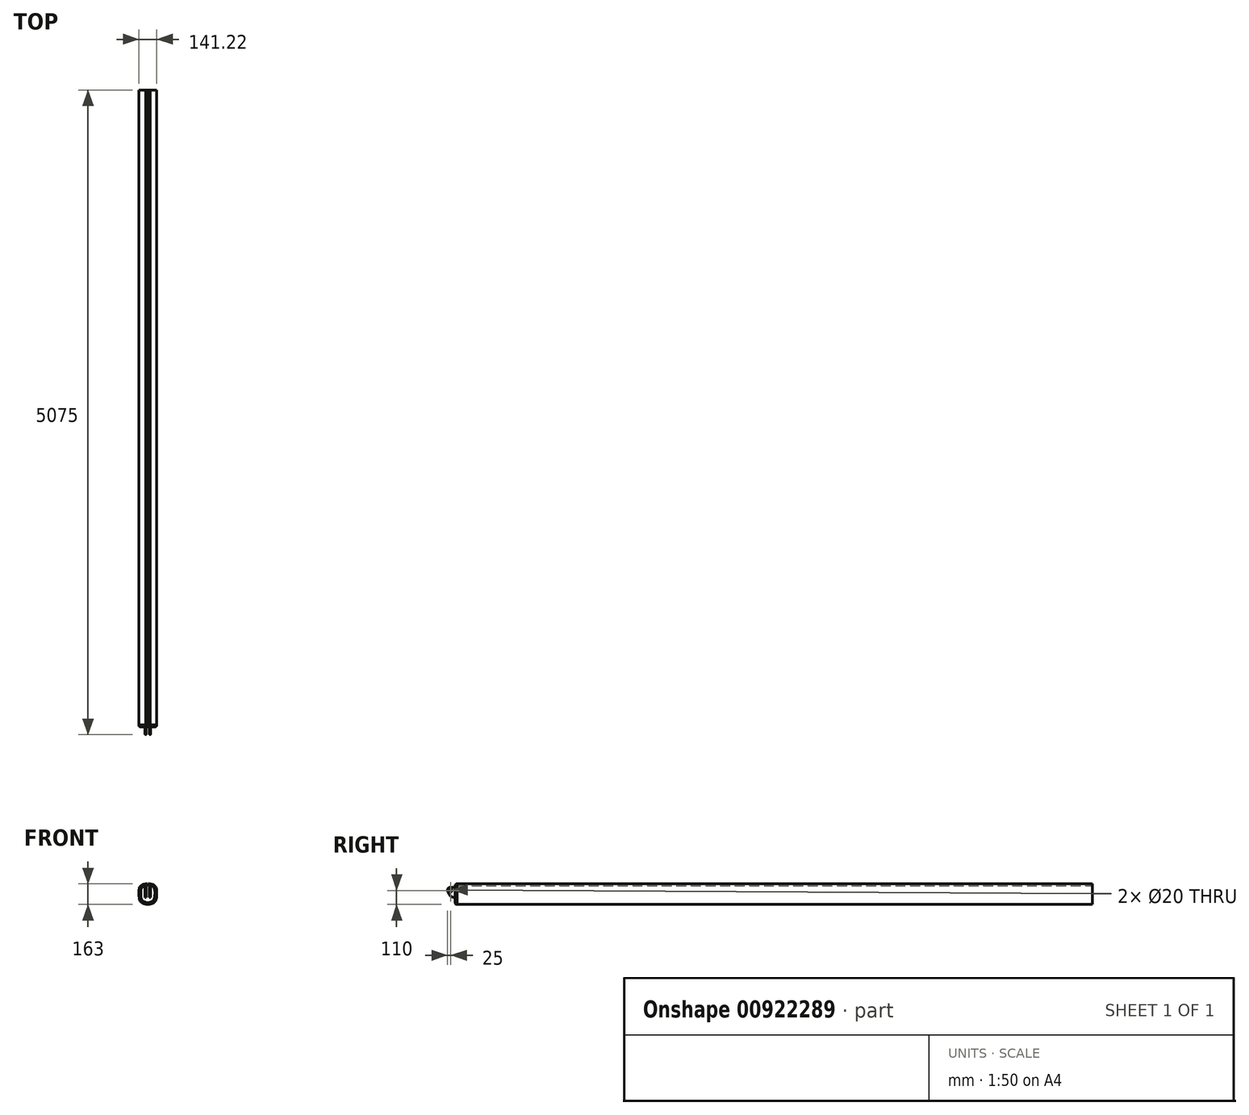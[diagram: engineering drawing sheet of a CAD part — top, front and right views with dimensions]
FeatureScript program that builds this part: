
annotation { "Feature Type Name" : "Feature", "Feature Type Description" : "" }
export const myFeature = defineFeature(function(context is Context, id is Id, definition is map)
    precondition{}
    {
        {
            var Q0;
            Q0=qCreatedBy(makeId("Front.planeOp"),FACE);
            var sketch = newSketch(context, id + "F0", { "sketchPlane" : qUnion([Q0])});
            skLineSegment(sketch, "E0", {"start": v(0, 75) * mm, "end": v(-5, 75) * mm});
            skLineSegment(sketch, "E1", {"start": v(-5, 75) * mm, "end": v(-5, 85) * mm});
            skLineSegment(sketch, "E2", {"start": v(-5, 85) * mm, "end": v(-2.5, 85) * mm});
            skLineSegment(sketch, "E3", {"start": v(-2.5, 85) * mm, "end": v(-2.5, 88) * mm});
            skLineSegment(sketch, "E4", {"start": v(-2.5, 88) * mm, "end": v(-17.5, 88) * mm});
            skFitSpline(sketch, "E5", {"points": [v(-17.5, 88) * mm, v(-62, 61.92) * mm, v(-70.21, 31.1) * mm, v(-64.87, -35.07) * mm, v(-48.84, -59.32) * mm, v(0, -75) * mm], "startDerivative": vector(-363.28, -8.37) * mm, "endDerivative": vector(330.1, 3.15) * mm});
            skLineSegment(sketch, "E6.MirrorCS", {"start": v(2.5, 85) * mm, "end": v(2.5, 88) * mm});
            skLineSegment(sketch, "E7.MirrorCS", {"start": v(5, 85) * mm, "end": v(2.5, 85) * mm});
            skLineSegment(sketch, "E8.MirrorCS", {"start": v(0, 75) * mm, "end": v(5, 75) * mm});
            skLineSegment(sketch, "E9.MirrorCS", {"start": v(2.5, 88) * mm, "end": v(17.5, 88) * mm});
            skLineSegment(sketch, "E10.MirrorCS", {"start": v(5, 75) * mm, "end": v(5, 85) * mm});
            skFitSpline(sketch, "E11.MirrorCS", {"points": [v(17.5, 88) * mm, v(62, 61.92) * mm, v(70.21, 31.1) * mm, v(64.87, -35.07) * mm, v(48.84, -59.32) * mm, v(0, -75) * mm], "startDerivative": vector(363.28, -8.37) * mm, "endDerivative": vector(-330.1, 3.15) * mm});
            skSolve(sketch);
        }
        {
            var Q0;
            Q0=makeQuery(id+"F0.imprint","IMPRINT",FACE,{"disambiguationData":[TD([[makeQuery(id+"F0.imprint","IMPRINT",EDGE,{"derivedFrom":sQuery(id+"F0.wireOp",EDGE,"E0")}),1.0]])]});
            extrude(context, id + "F1", {"entities" : qUnion([Q0]), "depth" : 5000 * mm, "offsetDistance" : 25 * mm, "symmetric" : true});
        }
        {
            var Q0;
            Q0=makeQuery(id+"F1.opExtrude","CAP_FACE",FACE,{"disambiguationData":[OSD([sQuery(id+"F0.wireOp",EDGE,"E0"),sQuery(id+"F0.wireOp",EDGE,"E1"),sQuery(id+"F0.wireOp",EDGE,"E2"),sQuery(id+"F0.wireOp",EDGE,"E3"),sQuery(id+"F0.wireOp",EDGE,"E4"),sQuery(id+"F0.wireOp",EDGE,"E5"),sQuery(id+"F0.wireOp",EDGE,"E6.MirrorCS"),sQuery(id+"F0.wireOp",EDGE,"E7.MirrorCS"),sQuery(id+"F0.wireOp",EDGE,"E8.MirrorCS"),sQuery(id+"F0.wireOp",EDGE,"E9.MirrorCS"),sQuery(id+"F0.wireOp",EDGE,"E10.MirrorCS"),sQuery(id+"F0.wireOp",EDGE,"E11.MirrorCS")])],"isStart":true});
            shell(context, id + "F2", {"entities" : qUnion([Q0]), "thickness" : 4 * mm});
        }
        {
            var Q0;
            Q0=makeQuery(id+"F1.opExtrude","CAP_FACE",FACE,{"disambiguationData":[OSD([sQuery(id+"F0.wireOp",EDGE,"E0"),sQuery(id+"F0.wireOp",EDGE,"E1"),sQuery(id+"F0.wireOp",EDGE,"E2"),sQuery(id+"F0.wireOp",EDGE,"E3"),sQuery(id+"F0.wireOp",EDGE,"E4"),sQuery(id+"F0.wireOp",EDGE,"E5"),sQuery(id+"F0.wireOp",EDGE,"E6.MirrorCS"),sQuery(id+"F0.wireOp",EDGE,"E7.MirrorCS"),sQuery(id+"F0.wireOp",EDGE,"E8.MirrorCS"),sQuery(id+"F0.wireOp",EDGE,"E9.MirrorCS"),sQuery(id+"F0.wireOp",EDGE,"E10.MirrorCS"),sQuery(id+"F0.wireOp",EDGE,"E11.MirrorCS")])],"isStart":false});
            extrude(context, id + "F3", {"entities" : qUnion([Q0]), "depth" : 15 * mm, "offsetDistance" : 25 * mm});
        }
        {
            var Q0;
            Q0=makeQuery(id+"F3.opExtrude","CAP_EDGE",EDGE,{"disambiguationData":[OSD([sQuery(id+"F0.wireOp",EDGE,"E11.MirrorCS")])],"isStart":false});
            var Q1;
            Q1=makeQuery(id+"F3.opExtrude","CAP_EDGE",EDGE,{"disambiguationData":[OSD([sQuery(id+"F0.wireOp",EDGE,"E5")])],"isStart":false});
            fillet(context, id + "F4", {"entities" : qUnion([Q0, Q1]), "radius" : 15 * mm, "tangentPropagation" : true, "allowEdgeOverflow" : false});
        }
        {
            var Q0;
            Q0=makeQuery(id+"F3.opExtrude","CAP_FACE",FACE,{"disambiguationData":[OSD([sQuery(id+"F0.wireOp",EDGE,"E0"),sQuery(id+"F0.wireOp",EDGE,"E1"),sQuery(id+"F0.wireOp",EDGE,"E2"),sQuery(id+"F0.wireOp",EDGE,"E3"),sQuery(id+"F0.wireOp",EDGE,"E4"),sQuery(id+"F0.wireOp",EDGE,"E5"),sQuery(id+"F0.wireOp",EDGE,"E6.MirrorCS"),sQuery(id+"F0.wireOp",EDGE,"E7.MirrorCS"),sQuery(id+"F0.wireOp",EDGE,"E8.MirrorCS"),sQuery(id+"F0.wireOp",EDGE,"E9.MirrorCS"),sQuery(id+"F0.wireOp",EDGE,"E10.MirrorCS"),sQuery(id+"F0.wireOp",EDGE,"E11.MirrorCS")])],"isStart":false});
            var sketch = newSketch(context, id + "F5", { "sketchPlane" : qUnion([Q0])});
            skSolve(sketch);
        }
        {
            var Q0;
            {var subQ0=sQuery(id+"F0.wireOp",EDGE,"E11.MirrorCS");var subQ1=sQuery(id+"F0.wireOp",EDGE,"E5");var subQ2=makeQuery(id+"F3.opExtrude","CAP_FACE",FACE,{"disambiguationData":[OSD([sQuery(id+"F0.wireOp",EDGE,"E0"),sQuery(id+"F0.wireOp",EDGE,"E1"),sQuery(id+"F0.wireOp",EDGE,"E2"),sQuery(id+"F0.wireOp",EDGE,"E3"),sQuery(id+"F0.wireOp",EDGE,"E4"),subQ1,sQuery(id+"F0.wireOp",EDGE,"E6.MirrorCS"),sQuery(id+"F0.wireOp",EDGE,"E7.MirrorCS"),sQuery(id+"F0.wireOp",EDGE,"E8.MirrorCS"),sQuery(id+"F0.wireOp",EDGE,"E9.MirrorCS"),sQuery(id+"F0.wireOp",EDGE,"E10.MirrorCS"),subQ0])],"isStart":false});Q0=makeQuery(id+"F5.imprint","IMPRINT",FACE,{"disambiguationData":[TD([[makeQuery(id+"F5.imprint","IMPRINT",EDGE,{"derivedFrom":makeQuery(id+"F4.opFillet","BLEND_EDGE",EDGE,{"blendedFrom":[makeQuery(id+"F3.opExtrude","CAP_EDGE",EDGE,{"disambiguationData":[OSD([subQ0])],"isStart":false}),subQ2],"blendedInto":[subQ2]})}),1.0]])]});}
            var sketch = newSketch(context, id + "F6", { "sketchPlane" : qUnion([Q0])});
            skLineSegment(sketch, "E12.bottom", {"start": v(-22.5, 60) * mm, "end": v(-12.5, 60) * mm});
            skLineSegment(sketch, "E12.top", {"start": v(-22.5, -20) * mm, "end": v(-12.5, -20) * mm});
            skLineSegment(sketch, "E12.left", {"start": v(-22.5, 60) * mm, "end": v(-22.5, -20) * mm});
            skLineSegment(sketch, "E12.right", {"start": v(-12.5, 60) * mm, "end": v(-12.5, -20) * mm});
            skLineSegment(sketch, "E13.bottom", {"start": v(12.5, 60) * mm, "end": v(22.5, 60) * mm});
            skLineSegment(sketch, "E13.top", {"start": v(12.5, -20) * mm, "end": v(22.5, -20) * mm});
            skLineSegment(sketch, "E13.left", {"start": v(12.5, 60) * mm, "end": v(12.5, -20) * mm});
            skLineSegment(sketch, "E13.right", {"start": v(22.5, 60) * mm, "end": v(22.5, -20) * mm});
            skSolve(sketch);
        }
        {
            var Q0;
            Q0 = qSketchRegion(id + "F6", true);
            extrude(context, id + "F7", {"entities" : qUnion([Q0]), "operationType" : NewBodyOperationType.ADD, "depth" : 60 * mm, "offsetDistance" : 25 * mm});
        }
        {
            var Q0;
            Q0=makeQuery(id+"F7.opExtrude","CAP_EDGE",EDGE,{"disambiguationData":[OSD([sQuery(id+"F6.wireOp",EDGE,"E12.bottom")])],"isStart":false});
            var Q1;
            Q1=makeQuery(id+"F7.opExtrude","CAP_EDGE",EDGE,{"disambiguationData":[OSD([sQuery(id+"F6.wireOp",EDGE,"E13.bottom")])],"isStart":false});
            fillet(context, id + "F8", {"entities" : qUnion([Q0, Q1]), "radius" : 20 * mm, "tangentPropagation" : true, "allowEdgeOverflow" : false});
        }
        {
            var Q0;
            Q0=makeQuery(id+"F7.opExtrude","CAP_EDGE",EDGE,{"disambiguationData":[OSD([sQuery(id+"F6.wireOp",EDGE,"E12.top")])],"isStart":false});
            var Q1;
            Q1=makeQuery(id+"F7.opExtrude","CAP_EDGE",EDGE,{"disambiguationData":[OSD([sQuery(id+"F6.wireOp",EDGE,"E13.top")])],"isStart":false});
            fillet(context, id + "F9", {"entities" : qUnion([Q0, Q1]), "radius" : 60 * mm, "tangentPropagation" : true, "allowEdgeOverflow" : false});
        }
        {
            var Q0;
            Q0=makeQuery(id+"F7.opExtrude","SWEPT_FACE",FACE,{"disambiguationData":[OSD([sQuery(id+"F6.wireOp",EDGE,"E13.right")])]});
            var sketch = newSketch(context, id + "F10", { "sketchPlane" : qUnion([Q0])});
            skCircle(sketch, "E14", {"center": v(-2550, 35) * mm, "radius": 10 * mm});
            skSolve(sketch);
        }
        {
            var Q0;
            Q0=makeQuery(id+"F10.imprint","IMPRINT",FACE,{"disambiguationData":[TD([[makeQuery(id+"F10.imprint","IMPRINT",EDGE,{"derivedFrom":sQuery(id+"F10.wireOp",EDGE,"E14")}),1.0]])]});
            extrude(context, id + "F11", {"entities" : qUnion([Q0]), "operationType" : NewBodyOperationType.REMOVE, "endBound" : BoundingType.THROUGH_ALL, "oppositeDirection" : true, "depth" : 25 * mm, "offsetDistance" : 25 * mm});
        }
    });
